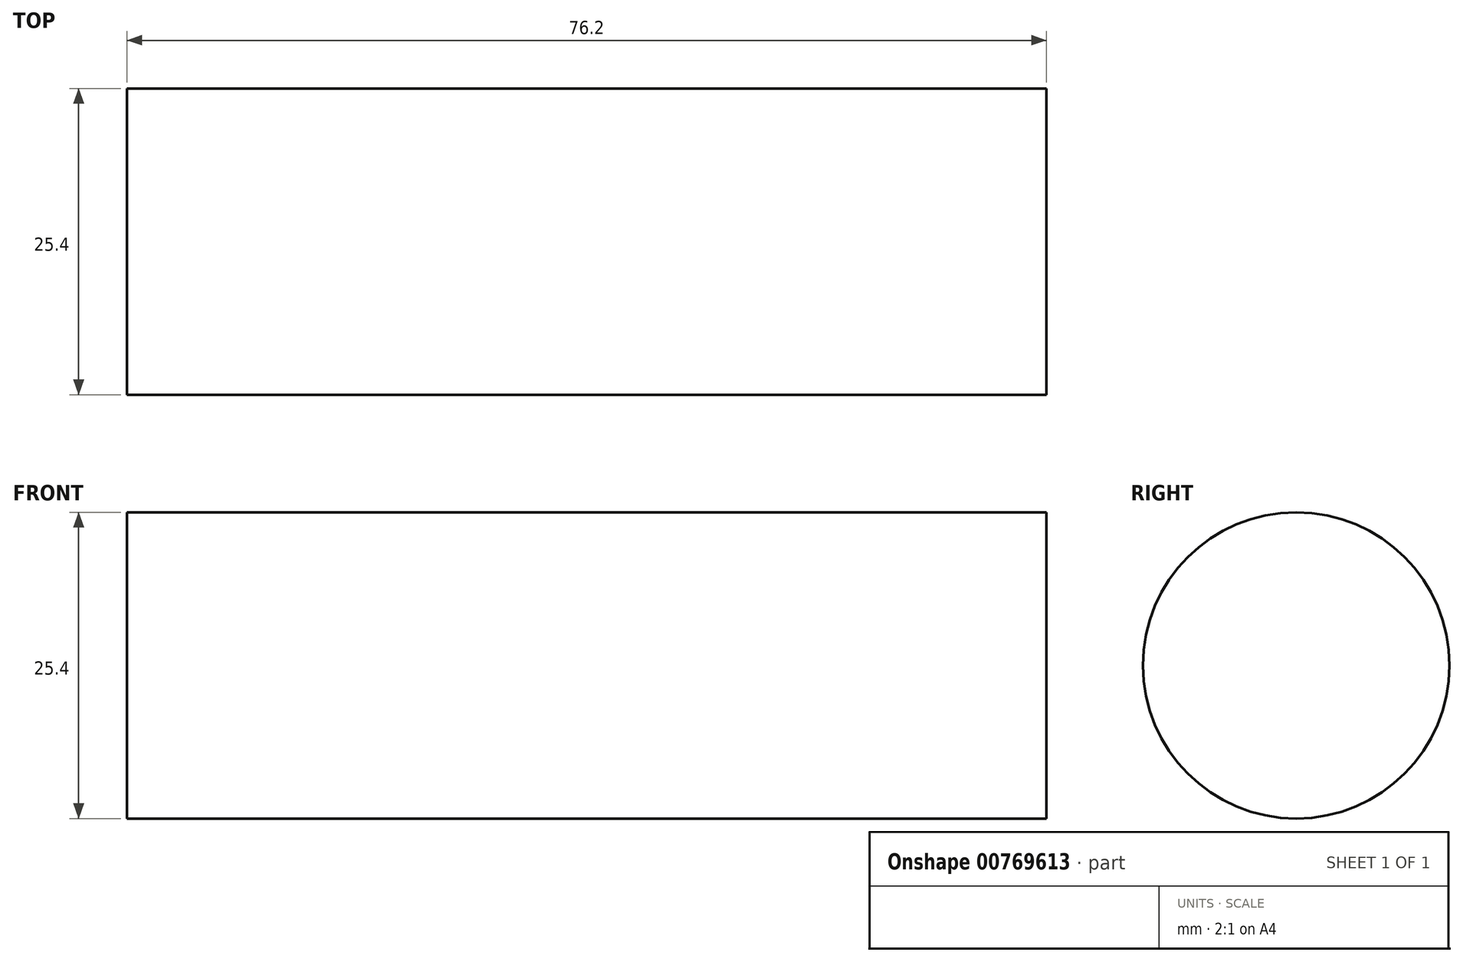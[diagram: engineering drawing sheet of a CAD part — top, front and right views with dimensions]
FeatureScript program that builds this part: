
annotation { "Feature Type Name" : "Feature", "Feature Type Description" : "" }
export const myFeature = defineFeature(function(context is Context, id is Id, definition is map)
    precondition{}
    {
        {
            var Q0;
            Q0=qCreatedBy(makeId("Right.planeOp"),FACE);
            var sketch = newSketch(context, id + "F0", { "sketchPlane" : qUnion([Q0])});
            skCircle(sketch, "E0", {"center": v(0, 0) * mm, "radius": 12.7 * mm});
            skSolve(sketch);
        }
        {
            var Q0;
            Q0 = qSketchRegion(id + "F0", true);
            extrude(context, id + "F1", {"entities" : qUnion([Q0]), "depth" : 76.2 * mm, "offsetDistance" : 25.4 * mm});
        }
    });
